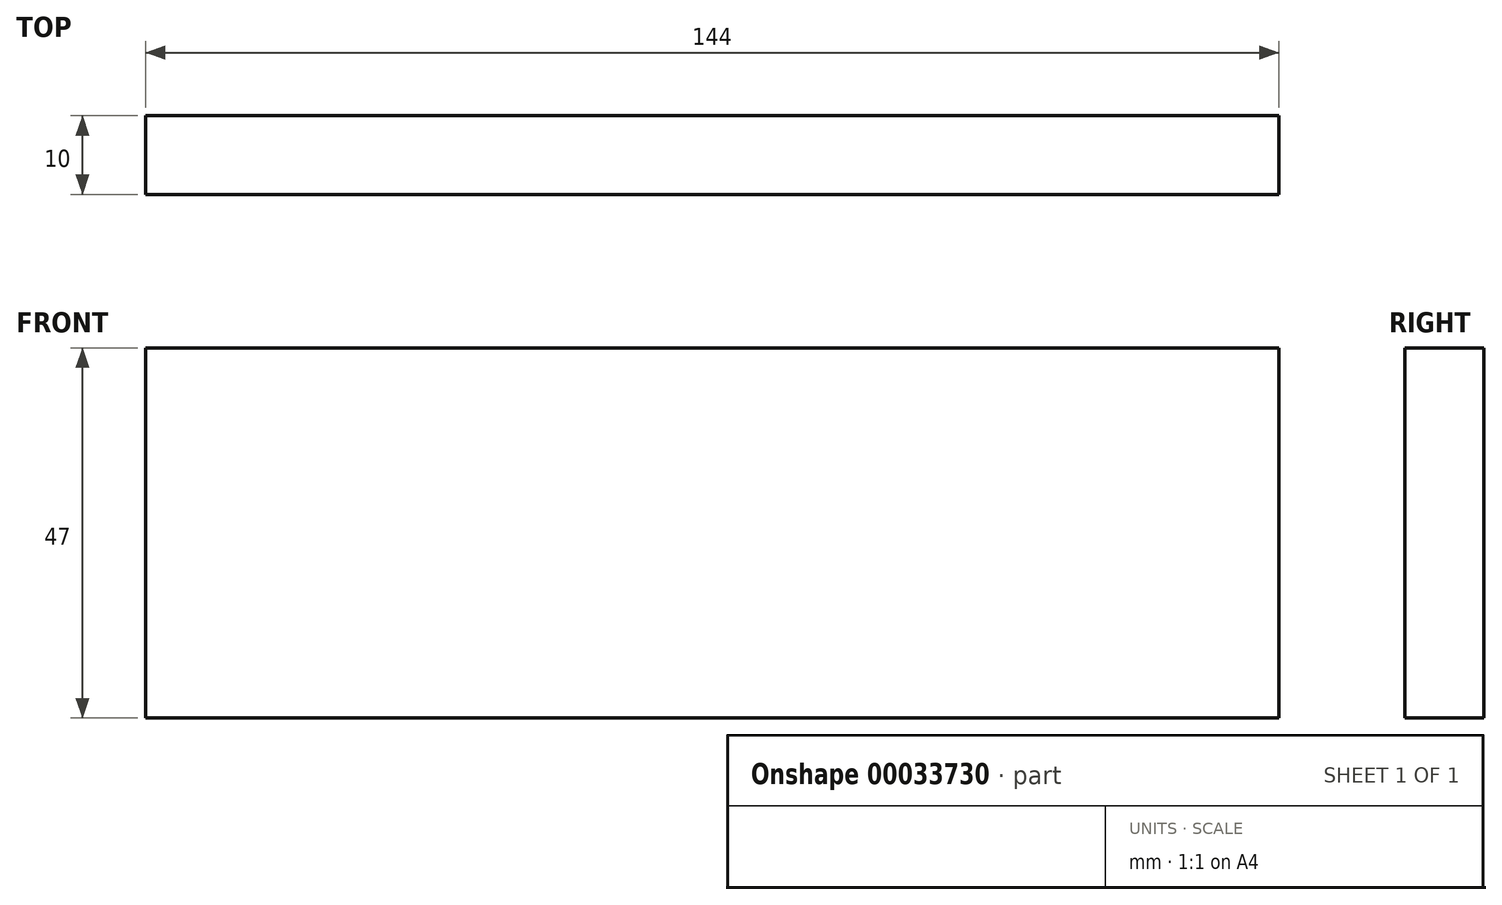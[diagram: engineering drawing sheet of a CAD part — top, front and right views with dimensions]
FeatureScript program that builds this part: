
annotation { "Feature Type Name" : "Feature", "Feature Type Description" : "" }
export const myFeature = defineFeature(function(context is Context, id is Id, definition is map)
    precondition{}
    {
        {
            var Q0;
            Q0=qCreatedBy(makeId("Front.planeOp"),FACE);
            var sketch = newSketch(context, id + "F0", { "sketchPlane" : qUnion([Q0])});
            skLineSegment(sketch, "E0.bottom", {"start": v(-72, 0) * mm, "end": v(72, 0) * mm});
            skLineSegment(sketch, "E0.top", {"start": v(-72, 47) * mm, "end": v(72, 47) * mm});
            skLineSegment(sketch, "E0.left", {"start": v(-72, 0) * mm, "end": v(-72, 47) * mm});
            skLineSegment(sketch, "E0.right", {"start": v(72, 0) * mm, "end": v(72, 47) * mm});
            skSolve(sketch);
        }
        {
            var Q0;
            Q0 = qSketchRegion(id + "F0", true);
            extrude(context, id + "F1", {"entities" : qUnion([Q0]), "depth" : 10 * mm});
        }
    });
